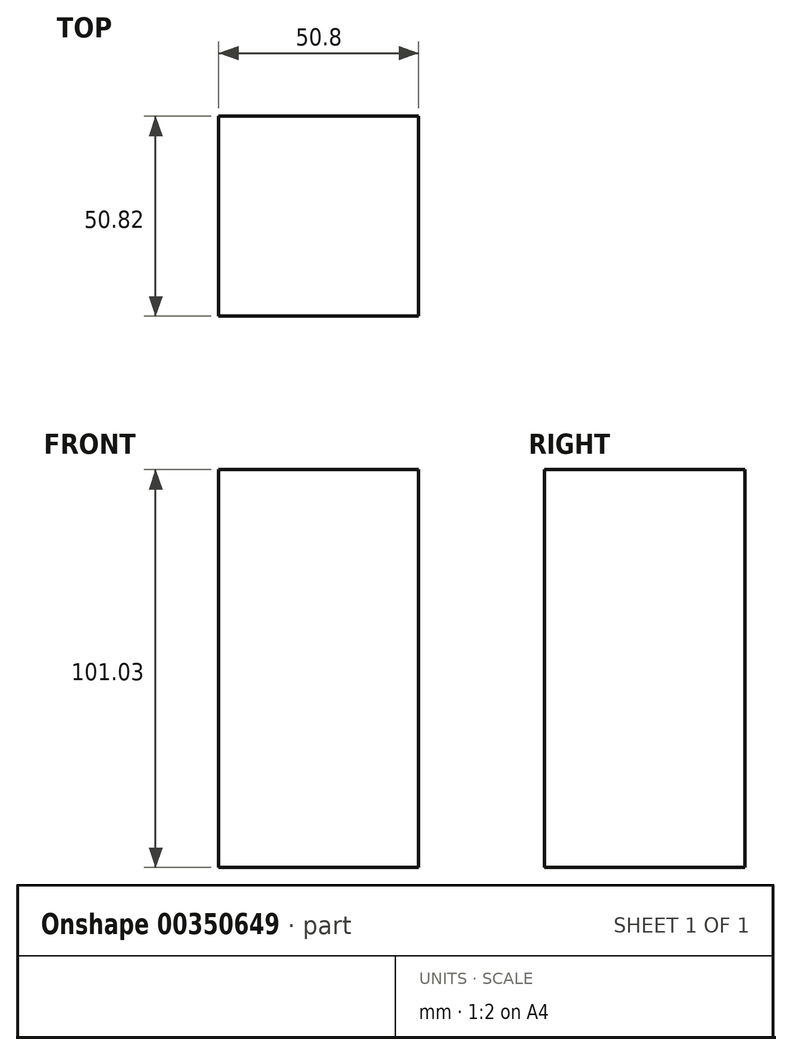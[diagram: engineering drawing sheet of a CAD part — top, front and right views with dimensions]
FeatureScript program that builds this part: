
annotation { "Feature Type Name" : "Feature", "Feature Type Description" : "" }
export const myFeature = defineFeature(function(context is Context, id is Id, definition is map)
    precondition{}
    {
        {
            var Q0;
            Q0=qCreatedBy(makeId("Right.planeOp"),FACE);
            var sketch = newSketch(context, id + "F0", { "sketchPlane" : qUnion([Q0])});
            skLineSegment(sketch, "E0.bottom", {"start": v(-37.96, 40.38) * mm, "end": v(12.86, 40.38) * mm});
            skLineSegment(sketch, "E0.top", {"start": v(-37.96, -60.65) * mm, "end": v(12.86, -60.65) * mm});
            skLineSegment(sketch, "E0.left", {"start": v(-37.96, 40.38) * mm, "end": v(-37.96, -60.65) * mm});
            skLineSegment(sketch, "E0.right", {"start": v(12.86, 40.38) * mm, "end": v(12.86, -60.65) * mm});
            skSolve(sketch);
        }
        {
            var Q0;
            Q0 = qSketchRegion(id + "F0", true);
            extrude(context, id + "F1", {"entities" : qUnion([Q0]), "oppositeDirection" : true, "depth" : 50.8 * mm});
        }
    });
